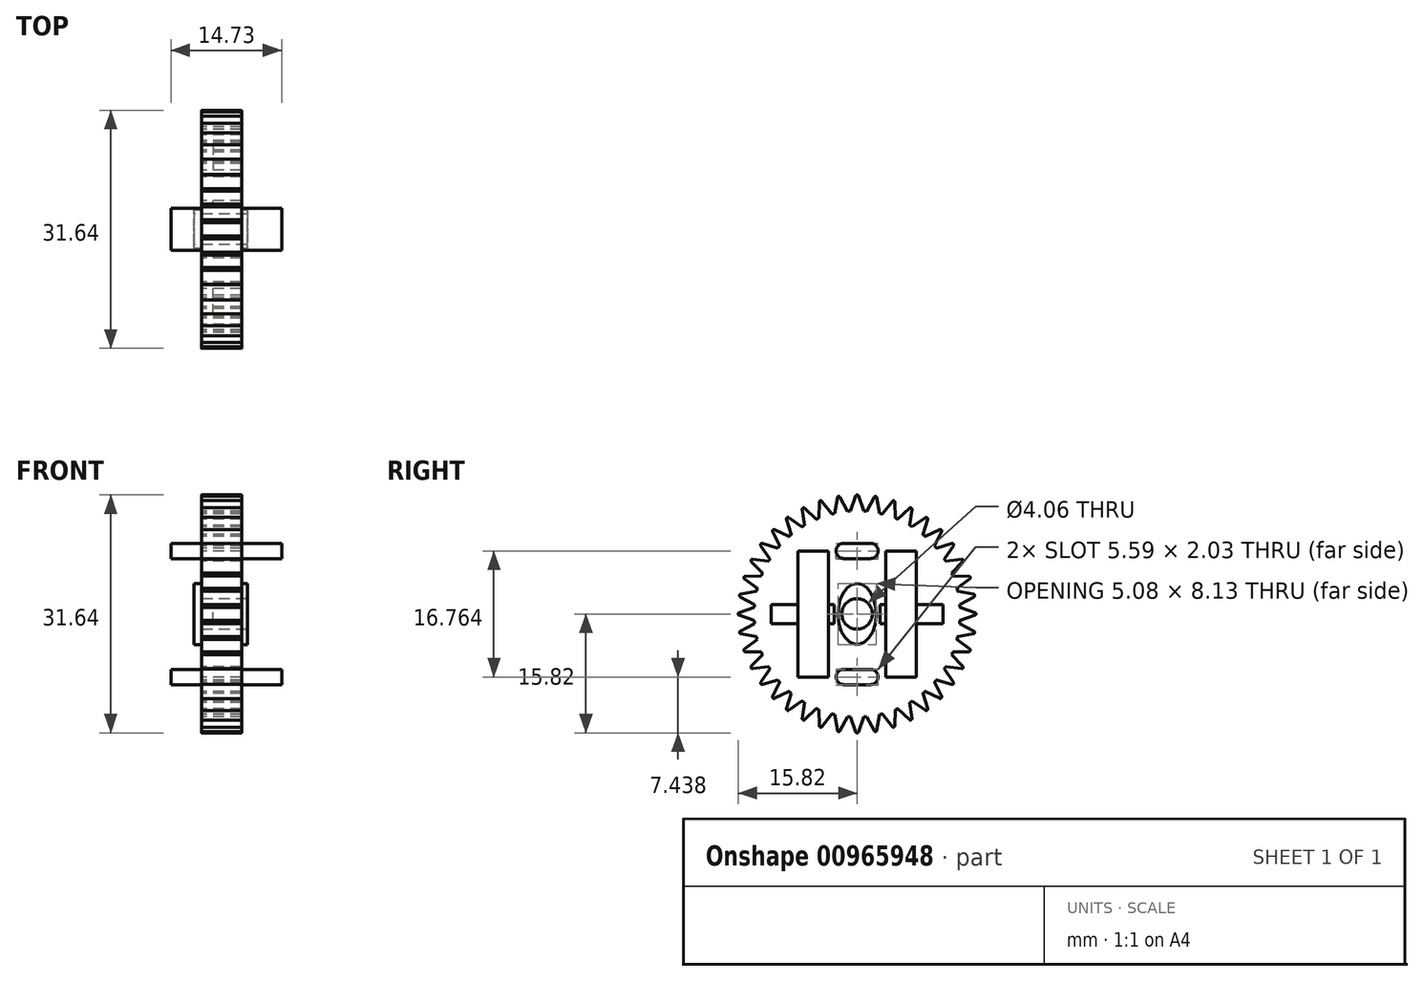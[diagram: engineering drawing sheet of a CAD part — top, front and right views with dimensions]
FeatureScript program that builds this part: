
annotation { "Feature Type Name" : "Feature", "Feature Type Description" : "" }
export const myFeature = defineFeature(function(context is Context, id is Id, definition is map)
    precondition{}
    {
        {
            var Q0;
            Q0=qCreatedBy(makeId("Right.planeOp"),FACE);
            var sketch = newSketch(context, id + "F0", { "sketchPlane" : qUnion([Q0])});
            skCircle(sketch, "E0", {"center": v(0, 0) * mm, "radius": 13.72 * mm});
            skLineSegment(sketch, "E1", {"start": v(-3.81, 0) * mm, "end": v(-3.81, 8.38) * mm});
            skLineSegment(sketch, "E2", {"start": v(-3.81, 0) * mm, "end": v(-3.81, -8.38) * mm});
            skLineSegment(sketch, "E3", {"start": v(3.8, 0) * mm, "end": v(3.8, 8.38) * mm});
            skLineSegment(sketch, "E4", {"start": v(3.8, 0) * mm, "end": v(3.8, -8.38) * mm});
            skLineSegment(sketch, "E5", {"start": v(-3.81, 8.38) * mm, "end": v(-7.87, 8.38) * mm});
            skLineSegment(sketch, "E6", {"start": v(-3.81, -8.38) * mm, "end": v(-7.87, -8.38) * mm});
            skLineSegment(sketch, "E7", {"start": v(3.8, -8.38) * mm, "end": v(7.87, -8.38) * mm});
            skLineSegment(sketch, "E8", {"start": v(3.8, 8.38) * mm, "end": v(7.87, 8.38) * mm});
            skLineSegment(sketch, "E9", {"start": v(7.87, 8.38) * mm, "end": v(7.87, -8.38) * mm});
            skLineSegment(sketch, "E10", {"start": v(-7.87, -8.38) * mm, "end": v(-7.87, 8.38) * mm});
            skLineSegment(sketch, "E11", {"start": v(0, 0) * mm, "end": v(0, 4.06) * mm});
            skLineSegment(sketch, "E12", {"start": v(0, 0) * mm, "end": v(0, -4.06) * mm});
            skLineSegment(sketch, "E13", {"start": v(0, 0) * mm, "end": v(2.54, 0) * mm});
            skLineSegment(sketch, "E14", {"start": v(0, 0) * mm, "end": v(-2.54, 0) * mm});
            skEllipse(sketch, "E15", {"center": v(0, 0) * mm, "majorRadius": 4.06 * mm, "minorRadius": 2.54 * mm, "majorAxis": v(0, 1)});
            skCircle(sketch, "E16", {"center": v(0, 0) * mm, "radius": 2.03 * mm});
            skLineSegment(sketch, "E17", {"start": v(-3.05, 0) * mm, "end": v(-3.05, 1.27) * mm});
            skLineSegment(sketch, "E18", {"start": v(-3.05, 0) * mm, "end": v(-3.05, -1.27) * mm});
            skLineSegment(sketch, "E19", {"start": v(-3.05, -1.27) * mm, "end": v(-3.81, -1.27) * mm});
            skLineSegment(sketch, "E20", {"start": v(-3.05, 1.27) * mm, "end": v(-3.81, 1.27) * mm});
            skLineSegment(sketch, "E21", {"start": v(3.05, 0) * mm, "end": v(3.05, 1.27) * mm});
            skLineSegment(sketch, "E22", {"start": v(3.05, 0) * mm, "end": v(3.05, -1.27) * mm});
            skLineSegment(sketch, "E23", {"start": v(3.05, 1.27) * mm, "end": v(3.8, 1.27) * mm});
            skLineSegment(sketch, "E24", {"start": v(3.05, -1.27) * mm, "end": v(3.8, -1.27) * mm});
            skLineSegment(sketch, "E25", {"start": v(11.43, 0) * mm, "end": v(11.43, 1.27) * mm});
            skLineSegment(sketch, "E26", {"start": v(11.43, 0) * mm, "end": v(11.43, -1.27) * mm});
            skLineSegment(sketch, "E27", {"start": v(11.43, 1.27) * mm, "end": v(7.87, 1.27) * mm});
            skLineSegment(sketch, "E28", {"start": v(11.43, -1.27) * mm, "end": v(7.87, -1.27) * mm});
            skLineSegment(sketch, "E29", {"start": v(-11.43, 0) * mm, "end": v(-11.43, -1.27) * mm});
            skLineSegment(sketch, "E30", {"start": v(-11.43, 0) * mm, "end": v(-11.43, 1.27) * mm});
            skLineSegment(sketch, "E31", {"start": v(-11.43, 1.27) * mm, "end": v(-7.87, 1.27) * mm});
            skLineSegment(sketch, "E32", {"start": v(-11.43, -1.27) * mm, "end": v(-7.87, -1.27) * mm});
            skLineSegment(sketch, "E33", {"start": v(0, 8.38) * mm, "end": v(-2.8, 8.38) * mm});
            skLineSegment(sketch, "E34", {"start": v(0, 8.38) * mm, "end": v(2.8, 8.38) * mm});
            skLineSegment(sketch, "E35", {"start": v(2.8, 8.38) * mm, "end": v(2.8, 9.4) * mm});
            skLineSegment(sketch, "E36", {"start": v(2.8, 8.38) * mm, "end": v(2.8, 7.37) * mm});
            skLineSegment(sketch, "E37", {"start": v(-2.8, 8.38) * mm, "end": v(-2.8, 9.4) * mm});
            skLineSegment(sketch, "E38", {"start": v(-2.8, 8.38) * mm, "end": v(-2.8, 7.37) * mm});
            skLineSegment(sketch, "E39", {"start": v(-2.8, 9.4) * mm, "end": v(2.8, 9.4) * mm});
            skLineSegment(sketch, "E40", {"start": v(-2.8, 7.37) * mm, "end": v(2.8, 7.37) * mm});
            skLineSegment(sketch, "E41", {"start": v(0, -8.38) * mm, "end": v(2.8, -8.38) * mm});
            skLineSegment(sketch, "E42", {"start": v(0, -8.38) * mm, "end": v(-2.8, -8.38) * mm});
            skLineSegment(sketch, "E43", {"start": v(-2.8, -8.38) * mm, "end": v(-2.8, -7.37) * mm});
            skLineSegment(sketch, "E44", {"start": v(-2.8, -8.38) * mm, "end": v(-2.8, -9.4) * mm});
            skLineSegment(sketch, "E45", {"start": v(2.8, -8.38) * mm, "end": v(2.8, -7.37) * mm});
            skLineSegment(sketch, "E46", {"start": v(2.8, -8.38) * mm, "end": v(2.8, -9.4) * mm});
            skLineSegment(sketch, "E47", {"start": v(-2.8, -9.4) * mm, "end": v(2.8, -9.4) * mm});
            skLineSegment(sketch, "E48", {"start": v(2.8, -7.37) * mm, "end": v(-2.8, -7.37) * mm});
            skSolve(sketch);
        }
        {
            var Q0;
            Q0=makeQuery(id+"F0.imprint","IMPRINT",FACE,{"disambiguationData":[TD([[makeQuery(id+"F0.imprint","IMPRINT",EDGE,{"derivedFrom":sQuery(id+"F0.wireOp",EDGE,"E0")}),1.0]])]});
            extrude(context, id + "F1", {"entities" : qUnion([Q0]), "depth" : 5.33 * mm, "offsetDistance" : 25.4 * mm});
        }
        {
            var Q0;
            {var subQ0=sQuery(id+"F0.wireOp",EDGE,"E15");var subQ1=sQuery(id+"F0.wireOp",EDGE,"E11");var subQ2=makeQuery(id+"F0.imprint","INTERSECT",VERTEX,{"derivedFrom":[subQ1,subQ0]});Q0=makeQuery(id+"F0.imprint","IMPRINT",FACE,{"disambiguationData":[TD([[makeQuery(id+"F0.imprint","IMPRINT",EDGE,{"disambiguationData":[TD([[subQ2,1.0]])],"derivedFrom":subQ1}),1.0]])]});}
            var Q1;
            {var subQ0=sQuery(id+"F0.wireOp",EDGE,"E15");var subQ1=sQuery(id+"F0.wireOp",EDGE,"E11");var subQ2=makeQuery(id+"F0.imprint","INTERSECT",VERTEX,{"derivedFrom":[subQ1,subQ0]});Q1=makeQuery(id+"F0.imprint","IMPRINT",FACE,{"disambiguationData":[TD([[makeQuery(id+"F0.imprint","IMPRINT",EDGE,{"disambiguationData":[TD([[subQ2,1.0]])],"derivedFrom":subQ1}),-1.0]])]});}
            var Q2;
            {var subQ0=sQuery(id+"F0.wireOp",EDGE,"E15");var subQ1=sQuery(id+"F0.wireOp",EDGE,"E12");var subQ2=makeQuery(id+"F0.imprint","INTERSECT",VERTEX,{"derivedFrom":[subQ1,subQ0]});Q2=makeQuery(id+"F0.imprint","IMPRINT",FACE,{"disambiguationData":[TD([[makeQuery(id+"F0.imprint","IMPRINT",EDGE,{"disambiguationData":[TD([[subQ2,1.0]])],"derivedFrom":subQ1}),1.0]])]});}
            var Q3;
            {var subQ0=sQuery(id+"F0.wireOp",EDGE,"E15");var subQ1=sQuery(id+"F0.wireOp",EDGE,"E12");var subQ2=makeQuery(id+"F0.imprint","INTERSECT",VERTEX,{"derivedFrom":[subQ1,subQ0]});Q3=makeQuery(id+"F0.imprint","IMPRINT",FACE,{"disambiguationData":[TD([[makeQuery(id+"F0.imprint","IMPRINT",EDGE,{"disambiguationData":[TD([[subQ2,1.0]])],"derivedFrom":subQ1}),-1.0]])]});}
            extrude(context, id + "F2", {"entities" : qUnion([Q0, Q1, Q2, Q3]), "operationType" : NewBodyOperationType.ADD, "depth" : 6.1 * mm, "offsetDistance" : 25.4 * mm, "hasSecondDirection" : true, "secondDirectionOppositeDirection" : true, "secondDirectionDepth" : 1.02 * mm});
        }
        {
            var Q0;
            Q0=makeQuery(id+"F0.imprint","IMPRINT",FACE,{"disambiguationData":[TD([[makeQuery(id+"F0.imprint","IMPRINT",EDGE,{"derivedFrom":sQuery(id+"F0.wireOp",EDGE,"E29")}),1.0]])]});
            var Q1;
            Q1=makeQuery(id+"F0.imprint","IMPRINT",FACE,{"disambiguationData":[TD([[makeQuery(id+"F0.imprint","IMPRINT",EDGE,{"derivedFrom":sQuery(id+"F0.wireOp",EDGE,"E25")}),1.0]])]});
            var Q2;
            Q2=makeQuery(id+"F0.imprint","IMPRINT",FACE,{"disambiguationData":[TD([[makeQuery(id+"F0.imprint","IMPRINT",EDGE,{"derivedFrom":sQuery(id+"F0.wireOp",EDGE,"E17")}),1.0]])]});
            var Q3;
            Q3=makeQuery(id+"F0.imprint","IMPRINT",FACE,{"disambiguationData":[TD([[makeQuery(id+"F0.imprint","IMPRINT",EDGE,{"derivedFrom":sQuery(id+"F0.wireOp",EDGE,"E21")}),-1.0]])]});
            extrude(context, id + "F3", {"entities" : qUnion([Q0, Q1, Q2, Q3]), "operationType" : NewBodyOperationType.ADD, "depth" : 1.52 * mm, "offsetDistance" : 25.4 * mm});
        }
        {
            var Q0;
            Q0=makeQuery(id+"F0.imprint","IMPRINT",FACE,{"disambiguationData":[TD([[makeQuery(id+"F0.imprint","IMPRINT",EDGE,{"derivedFrom":sQuery(id+"F0.wireOp",EDGE,"E33")}),-1.0]])]});
            var Q1;
            Q1=makeQuery(id+"F0.imprint","IMPRINT",FACE,{"disambiguationData":[TD([[makeQuery(id+"F0.imprint","IMPRINT",EDGE,{"derivedFrom":sQuery(id+"F0.wireOp",EDGE,"E41")}),-1.0]])]});
            var Q2;
            Q2=makeQuery(id+"F0.imprint","IMPRINT",FACE,{"disambiguationData":[TD([[makeQuery(id+"F0.imprint","IMPRINT",EDGE,{"derivedFrom":sQuery(id+"F0.wireOp",EDGE,"E41")}),1.0]])]});
            var Q3;
            Q3=makeQuery(id+"F0.imprint","IMPRINT",FACE,{"disambiguationData":[TD([[makeQuery(id+"F0.imprint","IMPRINT",EDGE,{"derivedFrom":sQuery(id+"F0.wireOp",EDGE,"E33")}),1.0]])]});
            extrude(context, id + "F4", {"entities" : qUnion([Q0, Q1, Q2, Q3]), "operationType" : NewBodyOperationType.ADD, "depth" : 10.67 * mm, "offsetDistance" : 25.4 * mm, "hasSecondDirection" : true, "secondDirectionOppositeDirection" : true, "secondDirectionDepth" : 4.06 * mm});
        }
        {
            var Q0;
            {var subQ0=sQuery(id+"F0.wireOp",EDGE,"E40");var subQ1=sQuery(id+"F0.wireOp",EDGE,"E39");var subQ2=sQuery(id+"F0.wireOp",EDGE,"E38");var subQ3=sQuery(id+"F0.wireOp",EDGE,"E37");var subQ4=sQuery(id+"F0.wireOp",EDGE,"E36");var subQ5=sQuery(id+"F0.wireOp",EDGE,"E35");Q0=makeQuery(id+"F4.boolean.opBoolean","SPLIT",EDGE,{"disambiguationData":[TD([makeQuery(id+"F4.opExtrude","CAP_FACE",FACE,{"disambiguationData":[OSD([subQ5,subQ4,subQ3,subQ2,subQ1,subQ0])],"isStart":false})])],"derivedFrom":makeQuery(id+"F4.opExtrude","SWEPT_EDGE",EDGE,{"disambiguationData":[OSD([subQ5,subQ1])]})});}
            var Q1;
            {var subQ0=sQuery(id+"F0.wireOp",EDGE,"E40");var subQ1=sQuery(id+"F0.wireOp",EDGE,"E39");var subQ2=sQuery(id+"F0.wireOp",EDGE,"E38");var subQ3=sQuery(id+"F0.wireOp",EDGE,"E37");var subQ4=sQuery(id+"F0.wireOp",EDGE,"E36");var subQ5=sQuery(id+"F0.wireOp",EDGE,"E35");Q1=makeQuery(id+"F4.boolean.opBoolean","SPLIT",EDGE,{"disambiguationData":[TD([makeQuery(id+"F4.opExtrude","CAP_FACE",FACE,{"disambiguationData":[OSD([subQ5,subQ4,subQ3,subQ2,subQ1,subQ0])],"isStart":false})])],"derivedFrom":makeQuery(id+"F4.opExtrude","SWEPT_EDGE",EDGE,{"disambiguationData":[OSD([subQ4,subQ0])]})});}
            var Q2;
            {var subQ0=sQuery(id+"F0.wireOp",EDGE,"E40");var subQ1=sQuery(id+"F0.wireOp",EDGE,"E39");var subQ2=sQuery(id+"F0.wireOp",EDGE,"E38");var subQ3=sQuery(id+"F0.wireOp",EDGE,"E37");var subQ4=sQuery(id+"F0.wireOp",EDGE,"E36");var subQ5=sQuery(id+"F0.wireOp",EDGE,"E35");Q2=makeQuery(id+"F4.boolean.opBoolean","SPLIT",EDGE,{"disambiguationData":[TD([makeQuery(id+"F4.opExtrude","CAP_FACE",FACE,{"disambiguationData":[OSD([subQ5,subQ4,subQ3,subQ2,subQ1,subQ0])],"isStart":false})])],"derivedFrom":makeQuery(id+"F4.opExtrude","SWEPT_EDGE",EDGE,{"disambiguationData":[OSD([subQ3,subQ1])]})});}
            var Q3;
            {var subQ0=sQuery(id+"F0.wireOp",EDGE,"E40");var subQ1=sQuery(id+"F0.wireOp",EDGE,"E39");var subQ2=sQuery(id+"F0.wireOp",EDGE,"E38");var subQ3=sQuery(id+"F0.wireOp",EDGE,"E37");var subQ4=sQuery(id+"F0.wireOp",EDGE,"E36");var subQ5=sQuery(id+"F0.wireOp",EDGE,"E35");Q3=makeQuery(id+"F4.boolean.opBoolean","SPLIT",EDGE,{"disambiguationData":[TD([makeQuery(id+"F4.opExtrude","CAP_FACE",FACE,{"disambiguationData":[OSD([subQ5,subQ4,subQ3,subQ2,subQ1,subQ0])],"isStart":false})])],"derivedFrom":makeQuery(id+"F4.opExtrude","SWEPT_EDGE",EDGE,{"disambiguationData":[OSD([subQ2,subQ0])]})});}
            var Q4;
            {var subQ0=sQuery(id+"F0.wireOp",EDGE,"E48");var subQ1=sQuery(id+"F0.wireOp",EDGE,"E47");var subQ2=sQuery(id+"F0.wireOp",EDGE,"E46");var subQ3=sQuery(id+"F0.wireOp",EDGE,"E45");var subQ4=sQuery(id+"F0.wireOp",EDGE,"E44");var subQ5=sQuery(id+"F0.wireOp",EDGE,"E43");Q4=makeQuery(id+"F4.boolean.opBoolean","SPLIT",EDGE,{"disambiguationData":[TD([makeQuery(id+"F4.opExtrude","CAP_FACE",FACE,{"disambiguationData":[OSD([subQ5,subQ4,subQ3,subQ2,subQ1,subQ0])],"isStart":false})])],"derivedFrom":makeQuery(id+"F4.opExtrude","SWEPT_EDGE",EDGE,{"disambiguationData":[OSD([subQ5,subQ0])]})});}
            var Q5;
            {var subQ0=sQuery(id+"F0.wireOp",EDGE,"E48");var subQ1=sQuery(id+"F0.wireOp",EDGE,"E47");var subQ2=sQuery(id+"F0.wireOp",EDGE,"E46");var subQ3=sQuery(id+"F0.wireOp",EDGE,"E45");var subQ4=sQuery(id+"F0.wireOp",EDGE,"E44");var subQ5=sQuery(id+"F0.wireOp",EDGE,"E43");Q5=makeQuery(id+"F4.boolean.opBoolean","SPLIT",EDGE,{"disambiguationData":[TD([makeQuery(id+"F4.opExtrude","CAP_FACE",FACE,{"disambiguationData":[OSD([subQ5,subQ4,subQ3,subQ2,subQ1,subQ0])],"isStart":false})])],"derivedFrom":makeQuery(id+"F4.opExtrude","SWEPT_EDGE",EDGE,{"disambiguationData":[OSD([subQ2,subQ1])]})});}
            var Q6;
            {var subQ0=sQuery(id+"F0.wireOp",EDGE,"E48");var subQ1=sQuery(id+"F0.wireOp",EDGE,"E47");var subQ2=sQuery(id+"F0.wireOp",EDGE,"E46");var subQ3=sQuery(id+"F0.wireOp",EDGE,"E45");var subQ4=sQuery(id+"F0.wireOp",EDGE,"E44");var subQ5=sQuery(id+"F0.wireOp",EDGE,"E43");Q6=makeQuery(id+"F4.boolean.opBoolean","SPLIT",EDGE,{"disambiguationData":[TD([makeQuery(id+"F4.opExtrude","CAP_FACE",FACE,{"disambiguationData":[OSD([subQ5,subQ4,subQ3,subQ2,subQ1,subQ0])],"isStart":false})])],"derivedFrom":makeQuery(id+"F4.opExtrude","SWEPT_EDGE",EDGE,{"disambiguationData":[OSD([subQ3,subQ0])]})});}
            var Q7;
            {var subQ0=sQuery(id+"F0.wireOp",EDGE,"E48");var subQ1=sQuery(id+"F0.wireOp",EDGE,"E47");var subQ2=sQuery(id+"F0.wireOp",EDGE,"E46");var subQ3=sQuery(id+"F0.wireOp",EDGE,"E45");var subQ4=sQuery(id+"F0.wireOp",EDGE,"E44");var subQ5=sQuery(id+"F0.wireOp",EDGE,"E43");Q7=makeQuery(id+"F4.boolean.opBoolean","SPLIT",EDGE,{"disambiguationData":[TD([makeQuery(id+"F4.opExtrude","CAP_FACE",FACE,{"disambiguationData":[OSD([subQ5,subQ4,subQ3,subQ2,subQ1,subQ0])],"isStart":false})])],"derivedFrom":makeQuery(id+"F4.opExtrude","SWEPT_EDGE",EDGE,{"disambiguationData":[OSD([subQ4,subQ1])]})});}
            fillet(context, id + "F5", {"entities" : qUnion([Q0, Q1, Q2, Q3, Q4, Q5, Q6, Q7]), "radius" : 1.02 * mm, "tangentPropagation" : true, "allowEdgeOverflow" : false});
        }
        {
            var Q0;
            Q0=qCreatedBy(makeId("Right.planeOp"),FACE);
            var sketch = newSketch(context, id + "F6", { "sketchPlane" : qUnion([Q0])});
            skLineSegment(sketch, "E49", {"start": v(-0.89, 13.66) * mm, "end": v(0.89, 13.66) * mm});
            skLineSegment(sketch, "E50", {"start": v(0, 13.66) * mm, "end": v(0, 16.2) * mm});
            skLineSegment(sketch, "E51", {"start": v(-0.89, 13.66) * mm, "end": v(0, 16.2) * mm});
            skLineSegment(sketch, "E52", {"start": v(0.89, 13.66) * mm, "end": v(0, 16.2) * mm});
            skSolve(sketch);
        }
        {
            var Q0;
            {var subQ2=sQuery(id+"F6.wireOp",EDGE,"E50");Q0=makeQuery(id+"F6.imprint","IMPRINT",FACE,{"disambiguationData":[TD([[makeQuery(id+"F6.imprint","IMPRINT",EDGE,{"derivedFrom":subQ2}),1.0]])]});}
            var Q1;
            {var subQ2=sQuery(id+"F6.wireOp",EDGE,"E50");Q1=makeQuery(id+"F6.imprint","IMPRINT",FACE,{"disambiguationData":[TD([[makeQuery(id+"F6.imprint","IMPRINT",EDGE,{"derivedFrom":subQ2}),-1.0]])]});}
            extrude(context, id + "F7", {"entities" : qUnion([Q0, Q1]), "depth" : 5.33 * mm, "offsetDistance" : 25.4 * mm});
        }
        {
            var Q0;
            Q0=makeQuery(id+"F7.opExtrude","SWEPT_EDGE",EDGE,{"disambiguationData":[OSD([sQuery(id+"F6.wireOp",EDGE,"E50"),sQuery(id+"F6.wireOp",EDGE,"E51"),sQuery(id+"F6.wireOp",EDGE,"E52")])]});
            fillet(context, id + "F8", {"entities" : qUnion([Q0]), "radius" : 0.19 * mm, "tangentPropagation" : true, "allowEdgeOverflow" : false});
        }
        {
            var Q0;
            Q0=makeQuery(id+"F7.opExtrude","SWEPT_BODY",BODY,{"disambiguationData":[OSD([sQuery(id+"F6.wireOp",EDGE,"E49"),sQuery(id+"F6.wireOp",EDGE,"E51"),sQuery(id+"F6.wireOp",EDGE,"E52")])]});
            var Q1;
            Q1=makeQuery(id+"F1.opExtrude","CAP_EDGE",EDGE,{"disambiguationData":[OSD([sQuery(id+"F0.wireOp",EDGE,"E0")])],"isStart":false});
            circularPattern(context, id + "F9", {"operationType" : NewBodyOperationType.ADD, "entities" : qUnion([Q0]), "axis" : qUnion([Q1]), "angle" : 360 * degree, "instanceCount" : 40, "equalSpace" : true});
        }
    });
